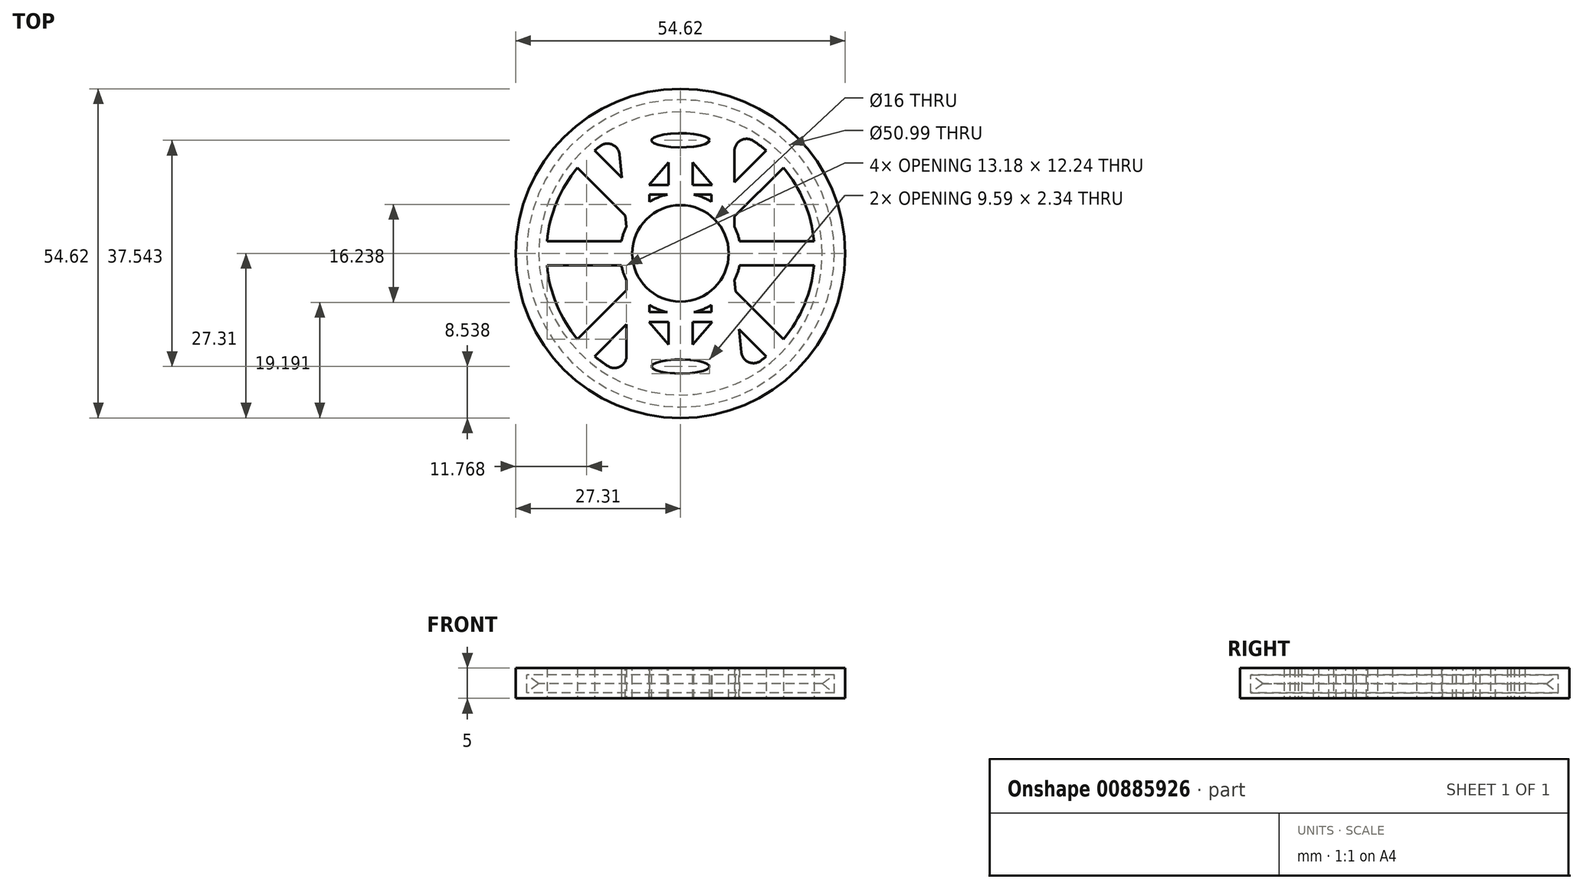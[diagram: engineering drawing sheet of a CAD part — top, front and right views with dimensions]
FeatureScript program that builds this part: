
annotation { "Feature Type Name" : "Feature", "Feature Type Description" : "" }
export const myFeature = defineFeature(function(context is Context, id is Id, definition is map)
    precondition{}
    {
        {
            var Q0;
            Q0=qCreatedBy(makeId("Top.planeOp"),FACE);
            var sketch = newSketch(context, id + "F0", { "sketchPlane" : qUnion([Q0])});
            skCircle(sketch, "E0", {"center": v(0, 0) * mm, "radius": 27.3 * mm});
            skCircle(sketch, "E1", {"center": v(0, 0) * mm, "radius": 3.12 * mm});
            skArc(sketch, "E2", {"start": v(-8.95, 4.46) * mm, "mid": v(-10, 0) * mm, "end": v(-8.95, -4.46) * mm});
            skArc(sketch, "E3.0", {"start": v(-13.28, 17.82) * mm, "mid": v(-22.21, -0.76) * mm, "end": v(-12.03, -18.69) * mm});
            skLineSegment(sketch, "E4.0", {"start": v(-10.1, 16.4) * mm, "end": v(-8.95, 4.46) * mm});
            skLineSegment(sketch, "E5.0", {"start": v(8.95, 17) * mm, "end": v(8.95, 4.46) * mm});
            skPoint(sketch, "E6.orphan", {"position": v(0, 22.46) * mm});
            skPoint(sketch, "E7.visualSharp", {"position": v(-10.4, 19.64) * mm});
            skArc(sketch, "E7.filletArc", {"start": v(-10.1, 16.4) * mm, "mid": v(-11.28, 18.04) * mm, "end": v(-13.28, 17.82) * mm});
            skPoint(sketch, "E8.visualSharp", {"position": v(8.95, 20.34) * mm});
            skArc(sketch, "E8.filletArc", {"start": v(12.03, 18.69) * mm, "mid": v(10, 18.76) * mm, "end": v(8.95, 17) * mm});
            skArc(sketch, "E9.1.0", {"start": v(-12.03, -18.69) * mm, "mid": v(-10, -18.76) * mm, "end": v(-8.95, -17) * mm});
            skArc(sketch, "E9.1.1", {"start": v(10.1, -16.4) * mm, "mid": v(11.28, -18.04) * mm, "end": v(13.28, -17.82) * mm});
            skLineSegment(sketch, "E9.1.2", {"start": v(10.1, -16.4) * mm, "end": v(8.95, -4.46) * mm});
            skLineSegment(sketch, "E9.1.3", {"start": v(-8.95, -17) * mm, "end": v(-8.95, -4.46) * mm});
            skArc(sketch, "E10.trimOffspring", {"start": v(13.28, -17.82) * mm, "mid": v(22.21, 0.76) * mm, "end": v(12.03, 18.69) * mm});
            skArc(sketch, "E11.trimOffspring", {"start": v(8.95, -4.46) * mm, "mid": v(10, 0) * mm, "end": v(8.95, 4.46) * mm});
            skSolve(sketch);
        }
        {
            var Q0;
            Q0=makeQuery(id+"F0.imprint","IMPRINT",FACE,{"disambiguationData":[TD([[makeQuery(id+"F0.imprint","IMPRINT",EDGE,{"derivedFrom":sQuery(id+"F0.wireOp",EDGE,"E0")}),1.0]])]});
            extrude(context, id + "F1", {"entities" : qUnion([Q0]), "depth" : 5 * mm, "offsetDistance" : 25.4 * mm});
        }
        {
            var Q0;
            Q0=makeQuery(id+"F1.opExtrude","CAP_FACE",FACE,{"disambiguationData":[OSD([sQuery(id+"F0.wireOp",EDGE,"E0"),sQuery(id+"F0.wireOp",EDGE,"E1"),sQuery(id+"F0.wireOp",EDGE,"E2"),sQuery(id+"F0.wireOp",EDGE,"E3.0"),sQuery(id+"F0.wireOp",EDGE,"E4.0"),sQuery(id+"F0.wireOp",EDGE,"E5.0"),sQuery(id+"F0.wireOp",EDGE,"E7.filletArc"),sQuery(id+"F0.wireOp",EDGE,"E8.filletArc"),sQuery(id+"F0.wireOp",EDGE,"E9.1.0"),sQuery(id+"F0.wireOp",EDGE,"E9.1.1"),sQuery(id+"F0.wireOp",EDGE,"E9.1.2"),sQuery(id+"F0.wireOp",EDGE,"E9.1.3"),sQuery(id+"F0.wireOp",EDGE,"E10.trimOffspring"),sQuery(id+"F0.wireOp",EDGE,"E11.trimOffspring")])],"isStart":false});
            var sketch = newSketch(context, id + "F2", { "sketchPlane" : qUnion([Q0])});
            skCircle(sketch, "E12", {"center": v(0, 0) * mm, "radius": 7.5 * mm});
            skSolve(sketch);
        }
        {
            var Q0;
            Q0=makeQuery(id+"F2.imprint","IMPRINT",FACE,{"disambiguationData":[TD([[makeQuery(id+"F2.imprint","IMPRINT",EDGE,{"derivedFrom":sQuery(id+"F2.wireOp",EDGE,"E12")}),1.0]])]});
            extrude(context, id + "F3", {"entities" : qUnion([Q0]), "operationType" : NewBodyOperationType.ADD, "depth" : 4 * mm, "offsetDistance" : 25.4 * mm});
        }
        {
            var Q0;
            Q0=qCreatedBy(makeId("Front.planeOp"),FACE);
            var sketch = newSketch(context, id + "F4", { "sketchPlane" : qUnion([Q0])});
            skCircle(sketch, "E13", {"center": v(-9.47, 12.31) * mm, "radius": 6.1 * mm});
            skLineSegment(sketch, "E14", {"start": v(0, 13.25) * mm, "end": v(0, -3.15) * mm, "construction": true});
            skSolve(sketch);
        }
        {
            var Q0;
            Q0=makeQuery(id+"F4.imprint","IMPRINT",FACE,{"disambiguationData":[TD([[makeQuery(id+"F4.imprint","IMPRINT",EDGE,{"derivedFrom":sQuery(id+"F4.wireOp",EDGE,"E13")}),1.0]])]});
            var Q1;
            Q1=sQuery(id+"F4.wireOp",EDGE,"E14");
            revolve(context, id + "F5", {"operationType" : NewBodyOperationType.REMOVE, "surfaceOperationType" : NewSurfaceOperationType.NEW, "entities" : qUnion([Q0]), "axis" : qUnion([Q1]), "revolveType" : RevolveType.FULL, "oppositeDirection" : true});
        }
        {
            var Q0;
            Q0=makeQuery(id+"F1.opExtrude","CAP_FACE",FACE,{"disambiguationData":[OSD([sQuery(id+"F0.wireOp",EDGE,"E0"),sQuery(id+"F0.wireOp",EDGE,"E1"),sQuery(id+"F0.wireOp",EDGE,"E2"),sQuery(id+"F0.wireOp",EDGE,"E3.0"),sQuery(id+"F0.wireOp",EDGE,"E4.0"),sQuery(id+"F0.wireOp",EDGE,"E5.0"),sQuery(id+"F0.wireOp",EDGE,"E7.filletArc"),sQuery(id+"F0.wireOp",EDGE,"E8.filletArc"),sQuery(id+"F0.wireOp",EDGE,"E9.1.0"),sQuery(id+"F0.wireOp",EDGE,"E9.1.1"),sQuery(id+"F0.wireOp",EDGE,"E9.1.2"),sQuery(id+"F0.wireOp",EDGE,"E9.1.3"),sQuery(id+"F0.wireOp",EDGE,"E10.trimOffspring"),sQuery(id+"F0.wireOp",EDGE,"E11.trimOffspring")])],"isStart":false});
            var sketch = newSketch(context, id + "F6", { "sketchPlane" : qUnion([Q0])});
            skLineSegment(sketch, "E15", {"start": v(0, 11.36) * mm, "end": v(-5.23, 11.36) * mm});
            skLineSegment(sketch, "E16", {"start": v(-5.23, 11.36) * mm, "end": v(0, 17.41) * mm});
            skLineSegment(sketch, "E17", {"start": v(0, 17.41) * mm, "end": v(0, 11.36) * mm});
            skLineSegment(sketch, "E18.MirrorCS", {"start": v(0, 11.36) * mm, "end": v(5.23, 11.36) * mm});
            skLineSegment(sketch, "E19.MirrorCS", {"start": v(5.23, 11.36) * mm, "end": v(0, 17.41) * mm});
            skLineSegment(sketch, "E20.1.0", {"start": v(-5.23, -11.36) * mm, "end": v(0, -17.41) * mm});
            skLineSegment(sketch, "E20.1.1", {"start": v(5.23, -11.36) * mm, "end": v(0, -17.41) * mm});
            skLineSegment(sketch, "E20.1.2", {"start": v(0, -11.36) * mm, "end": v(-5.23, -11.36) * mm});
            skLineSegment(sketch, "E20.1.3", {"start": v(0, -11.36) * mm, "end": v(5.23, -11.36) * mm});
            skPoint(sketch, "E20.center", {"position": v(0, 0) * mm});
            skSolve(sketch);
        }
        {
            var Q0;
            Q0=makeQuery(id+"F6.imprint","IMPRINT",FACE,{"disambiguationData":[TD([[makeQuery(id+"F6.imprint","IMPRINT",EDGE,{"derivedFrom":sQuery(id+"F6.wireOp",EDGE,"E17")}),1.0]])]});
            var Q1;
            Q1=makeQuery(id+"F6.imprint","IMPRINT",FACE,{"disambiguationData":[TD([[makeQuery(id+"F6.imprint","IMPRINT",EDGE,{"derivedFrom":sQuery(id+"F6.wireOp",EDGE,"E15")}),-1.0]])]});
            var Q2;
            Q2=makeQuery(id+"F6.imprint","IMPRINT",FACE,{"disambiguationData":[TD([[makeQuery(id+"F6.imprint","IMPRINT",EDGE,{"derivedFrom":sQuery(id+"F6.wireOp",EDGE,"E20.1.0")}),1.0]])]});
            extrude(context, id + "F7", {"entities" : qUnion([Q0, Q1, Q2]), "operationType" : NewBodyOperationType.REMOVE, "endBound" : BoundingType.THROUGH_ALL, "oppositeDirection" : true, "depth" : 25.4 * mm, "offsetDistance" : 25.4 * mm});
        }
        {
            var Q0;
            Q0=qCreatedBy(makeId("Front.planeOp"),FACE);
            var sketch = newSketch(context, id + "F8", { "sketchPlane" : qUnion([Q0])});
            skLineSegment(sketch, "E21", {"start": v(-25.5, 2.4) * mm, "end": v(-23.5, 2.4) * mm});
            skLineSegment(sketch, "E22", {"start": v(-23.5, 2.4) * mm, "end": v(-25.5, 0.9) * mm});
            skLineSegment(sketch, "E23", {"start": v(-25.5, 0.9) * mm, "end": v(-25.5, 2.4) * mm});
            skLineSegment(sketch, "E24.MirrorCS", {"start": v(-23.5, 2.4) * mm, "end": v(-25.5, 3.9) * mm});
            skLineSegment(sketch, "E25.MirrorCS", {"start": v(-25.5, 3.9) * mm, "end": v(-25.5, 2.4) * mm});
            skLineSegment(sketch, "E26", {"start": v(0, 41.08) * mm, "end": v(0, 0) * mm, "construction": true});
            skSolve(sketch);
        }
        {
            var Q0;
            Q0=qSketchRegion(id+"F8",true);
            var Q1;
            Q1=sQuery(id+"F8.wireOp",EDGE,"E26");
            revolve(context, id + "F9", {"operationType" : NewBodyOperationType.REMOVE, "surfaceOperationType" : NewSurfaceOperationType.NEW, "entities" : qUnion([Q0]), "axis" : qUnion([Q1]), "revolveType" : RevolveType.FULL});
        }
        {
            var Q0;
            Q0=makeQuery(id+"F0.imprint","IMPRINT",FACE,{"disambiguationData":[TD([[makeQuery(id+"F0.imprint","IMPRINT",EDGE,{"derivedFrom":sQuery(id+"F0.wireOp",EDGE,"E5.0")}),1.0]])]});
            var sketch = newSketch(context, id + "F10", { "sketchPlane" : qUnion([Q0])});
            skCircle(sketch, "E27", {"center": v(0, 5.74) * mm, "radius": 0.66 * mm});
            skCircle(sketch, "E28.1.0", {"center": v(-4.06, 4.06) * mm, "radius": 0.66 * mm});
            skCircle(sketch, "E28.2.0", {"center": v(-5.74, 0) * mm, "radius": 0.66 * mm});
            skPoint(sketch, "E28.center", {"position": v(0, 0) * mm});
            skCircle(sketch, "E29.1.3.0", {"center": v(-4.06, -4.06) * mm, "radius": 0.66 * mm});
            skCircle(sketch, "E29.1.4.0", {"center": v(0, -5.74) * mm, "radius": 0.66 * mm});
            skCircle(sketch, "E29.1.5.0", {"center": v(4.06, -4.06) * mm, "radius": 0.66 * mm});
            skCircle(sketch, "E29.1.6.0", {"center": v(5.74, 0) * mm, "radius": 0.66 * mm});
            skCircle(sketch, "E30.1.7.0", {"center": v(4.06, 4.06) * mm, "radius": 0.66 * mm});
            skSolve(sketch);
        }
        {
            var Q0;
            Q0=qSketchRegion(id+"F10",true);
            extrude(context, id + "F11", {"entities" : qUnion([Q0]), "operationType" : NewBodyOperationType.REMOVE, "endBound" : BoundingType.THROUGH_ALL, "depth" : 25.4 * mm, "offsetDistance" : 25.4 * mm});
        }
        {
            var Q0;
            Q0=qCreatedBy(makeId("Top.planeOp"),FACE);
            var sketch = newSketch(context, id + "F12", { "sketchPlane" : qUnion([Q0])});
            skLineSegment(sketch, "E31.0", {"start": v(-22.45, -2) * mm, "end": v(-8.8, -2) * mm});
            skLineSegment(sketch, "E32.0", {"start": v(-22.45, 2) * mm, "end": v(-8.8, 2) * mm});
            skPoint(sketch, "E33.start.orphan", {"position": v(-22.45, 0) * mm});
            skLineSegment(sketch, "E34", {"start": v(-8.8, -2) * mm, "end": v(-8.8, 2) * mm});
            skLineSegment(sketch, "E35", {"start": v(-22.45, -2) * mm, "end": v(-22.45, 2) * mm});
            skLineSegment(sketch, "E36.1.0", {"start": v(-4.8, -7.64) * mm, "end": v(-7.64, -4.8) * mm});
            skLineSegment(sketch, "E36.1.1", {"start": v(-14.46, -17.29) * mm, "end": v(-4.8, -7.64) * mm});
            skLineSegment(sketch, "E36.1.2", {"start": v(-17.29, -14.46) * mm, "end": v(-7.64, -4.8) * mm});
            skLineSegment(sketch, "E36.1.3", {"start": v(-14.46, -17.29) * mm, "end": v(-17.29, -14.46) * mm});
            skLineSegment(sketch, "E36.2.0", {"start": v(2, -8.8) * mm, "end": v(-2, -8.8) * mm});
            skLineSegment(sketch, "E36.2.1", {"start": v(2, -22.45) * mm, "end": v(2, -8.8) * mm});
            skLineSegment(sketch, "E36.2.2", {"start": v(-2, -22.45) * mm, "end": v(-2, -8.8) * mm});
            skLineSegment(sketch, "E36.2.3", {"start": v(2, -22.45) * mm, "end": v(-2, -22.45) * mm});
            skPoint(sketch, "E36.center", {"position": v(0, 0) * mm});
            skLineSegment(sketch, "E37.1.3.0", {"start": v(7.64, -4.8) * mm, "end": v(4.8, -7.64) * mm});
            skLineSegment(sketch, "E37.3.3.0", {"start": v(17.29, -14.46) * mm, "end": v(7.64, -4.8) * mm});
            skLineSegment(sketch, "E37.6.3.0", {"start": v(14.46, -17.29) * mm, "end": v(4.8, -7.64) * mm});
            skLineSegment(sketch, "E37.9.3.0", {"start": v(17.29, -14.46) * mm, "end": v(14.46, -17.29) * mm});
            skLineSegment(sketch, "E38.1.4.0", {"start": v(8.8, 2) * mm, "end": v(8.8, -2) * mm});
            skLineSegment(sketch, "E38.3.4.0", {"start": v(22.45, 2) * mm, "end": v(8.8, 2) * mm});
            skLineSegment(sketch, "E38.6.4.0", {"start": v(22.45, -2) * mm, "end": v(8.8, -2) * mm});
            skLineSegment(sketch, "E38.9.4.0", {"start": v(22.45, 2) * mm, "end": v(22.45, -2) * mm});
            skLineSegment(sketch, "E38.1.5.0", {"start": v(4.8, 7.64) * mm, "end": v(7.64, 4.8) * mm});
            skLineSegment(sketch, "E38.3.5.0", {"start": v(14.46, 17.29) * mm, "end": v(4.8, 7.64) * mm});
            skLineSegment(sketch, "E38.6.5.0", {"start": v(17.29, 14.46) * mm, "end": v(7.64, 4.8) * mm});
            skLineSegment(sketch, "E38.9.5.0", {"start": v(14.46, 17.29) * mm, "end": v(17.29, 14.46) * mm});
            skLineSegment(sketch, "E39.1.6.0", {"start": v(-2, 8.8) * mm, "end": v(2, 8.8) * mm});
            skLineSegment(sketch, "E39.3.6.0", {"start": v(-2, 22.45) * mm, "end": v(-2, 8.8) * mm});
            skLineSegment(sketch, "E39.6.6.0", {"start": v(2, 22.45) * mm, "end": v(2, 8.8) * mm});
            skLineSegment(sketch, "E39.9.6.0", {"start": v(-2, 22.45) * mm, "end": v(2, 22.45) * mm});
            skLineSegment(sketch, "E39.1.7.0", {"start": v(-7.64, 4.8) * mm, "end": v(-4.8, 7.64) * mm});
            skLineSegment(sketch, "E39.3.7.0", {"start": v(-17.29, 14.46) * mm, "end": v(-7.64, 4.8) * mm});
            skLineSegment(sketch, "E39.6.7.0", {"start": v(-14.46, 17.29) * mm, "end": v(-4.8, 7.64) * mm});
            skLineSegment(sketch, "E39.9.7.0", {"start": v(-17.29, 14.46) * mm, "end": v(-14.46, 17.29) * mm});
            skSolve(sketch);
        }
        {
            var Q0;
            Q0=qSketchRegion(id+"F12",true);
            extrude(context, id + "F13", {"entities" : qUnion([Q0]), "operationType" : NewBodyOperationType.ADD, "depth" : 5 * mm, "offsetDistance" : 25.4 * mm});
        }
        {
            var Q0;
            Q0=qCreatedBy(makeId("Top.planeOp"),FACE);
            var sketch = newSketch(context, id + "F14", { "sketchPlane" : qUnion([Q0])});
            skEllipse(sketch, "E40", {"center": v(0, 18.77) * mm, "majorRadius": 4.8 * mm, "minorRadius": 1.17 * mm, "majorAxis": v(1, 0)});
            skEllipse(sketch, "E41.1.0", {"center": v(0, -18.77) * mm, "majorRadius": 4.8 * mm, "minorRadius": 1.17 * mm, "majorAxis": v(-1, 0)});
            skPoint(sketch, "E41.center", {"position": v(0, 0) * mm});
            skSolve(sketch);
        }
        {
            var Q0;
            Q0=qSketchRegion(id+"F14",true);
            extrude(context, id + "F15", {"entities" : qUnion([Q0]), "operationType" : NewBodyOperationType.REMOVE, "endBound" : BoundingType.SYMMETRIC, "oppositeDirection" : true, "depth" : 25.4 * mm, "offsetDistance" : 25.4 * mm});
        }
        {
            var Q0;
            Q0=qCreatedBy(makeId("Top.planeOp"),FACE);
            var sketch = newSketch(context, id + "F16", { "sketchPlane" : qUnion([Q0])});
            skLineSegment(sketch, "E42.bottom", {"start": v(5.15, 9.76) * mm, "end": v(-5.15, 9.76) * mm});
            skLineSegment(sketch, "E42.top", {"start": v(5.15, 8.51) * mm, "end": v(-5.15, 8.51) * mm});
            skLineSegment(sketch, "E42.left", {"start": v(5.15, 9.76) * mm, "end": v(5.15, 8.51) * mm});
            skLineSegment(sketch, "E42.right", {"start": v(-5.15, 9.76) * mm, "end": v(-5.15, 8.51) * mm});
            skPoint(sketch, "E42.middle", {"position": v(0, 9.13) * mm});
            skLineSegment(sketch, "E43.1.0", {"start": v(-5.15, -9.76) * mm, "end": v(-5.15, -8.51) * mm});
            skLineSegment(sketch, "E43.1.1", {"start": v(5.15, -9.76) * mm, "end": v(5.15, -8.51) * mm});
            skLineSegment(sketch, "E43.1.2", {"start": v(-5.15, -8.51) * mm, "end": v(5.15, -8.51) * mm});
            skLineSegment(sketch, "E43.1.3", {"start": v(-5.15, -9.76) * mm, "end": v(5.15, -9.76) * mm});
            skPoint(sketch, "E43.center", {"position": v(0, 0) * mm});
            skSolve(sketch);
        }
        {
            var Q0;
            Q0=qSketchRegion(id+"F16",true);
            extrude(context, id + "F17", {"entities" : qUnion([Q0]), "operationType" : NewBodyOperationType.REMOVE, "endBound" : BoundingType.SYMMETRIC, "oppositeDirection" : true, "depth" : 25.4 * mm, "offsetDistance" : 25.4 * mm});
        }
        {
            var Q0;
            Q0=makeQuery(id+"F13.boolean.opBoolean","MERGE",FACE,{"derivedFrom":[makeQuery(id+"F1.opExtrude","CAP_FACE",FACE,{"disambiguationData":[OSD([sQuery(id+"F0.wireOp",EDGE,"E0"),sQuery(id+"F0.wireOp",EDGE,"E1"),sQuery(id+"F0.wireOp",EDGE,"E2"),sQuery(id+"F0.wireOp",EDGE,"E3.0"),sQuery(id+"F0.wireOp",EDGE,"E4.0"),sQuery(id+"F0.wireOp",EDGE,"E5.0"),sQuery(id+"F0.wireOp",EDGE,"E7.filletArc"),sQuery(id+"F0.wireOp",EDGE,"E8.filletArc"),sQuery(id+"F0.wireOp",EDGE,"E9.1.0"),sQuery(id+"F0.wireOp",EDGE,"E9.1.1"),sQuery(id+"F0.wireOp",EDGE,"E9.1.2"),sQuery(id+"F0.wireOp",EDGE,"E9.1.3"),sQuery(id+"F0.wireOp",EDGE,"E10.trimOffspring"),sQuery(id+"F0.wireOp",EDGE,"E11.trimOffspring")])],"isStart":false}),makeQuery(id+"F13.opExtrude","CAP_FACE",FACE,{"disambiguationData":[OSD([sQuery(id+"F12.wireOp",EDGE,"E31.0"),sQuery(id+"F12.wireOp",EDGE,"E32.0"),sQuery(id+"F12.wireOp",EDGE,"E34"),sQuery(id+"F12.wireOp",EDGE,"E35")])],"isStart":false}),makeQuery(id+"F13.opExtrude","CAP_FACE",FACE,{"disambiguationData":[OSD([sQuery(id+"F12.wireOp",EDGE,"E36.1.0"),sQuery(id+"F12.wireOp",EDGE,"E36.1.1"),sQuery(id+"F12.wireOp",EDGE,"E36.1.2"),sQuery(id+"F12.wireOp",EDGE,"E36.1.3")])],"isStart":false}),makeQuery(id+"F13.opExtrude","CAP_FACE",FACE,{"disambiguationData":[OSD([sQuery(id+"F12.wireOp",EDGE,"E36.2.0"),sQuery(id+"F12.wireOp",EDGE,"E36.2.1"),sQuery(id+"F12.wireOp",EDGE,"E36.2.2"),sQuery(id+"F12.wireOp",EDGE,"E36.2.3")])],"isStart":false}),makeQuery(id+"F13.opExtrude","CAP_FACE",FACE,{"disambiguationData":[OSD([sQuery(id+"F12.wireOp",EDGE,"E37.1.3.0"),sQuery(id+"F12.wireOp",EDGE,"E37.3.3.0"),sQuery(id+"F12.wireOp",EDGE,"E37.6.3.0"),sQuery(id+"F12.wireOp",EDGE,"E37.9.3.0")])],"isStart":false}),makeQuery(id+"F13.opExtrude","CAP_FACE",FACE,{"disambiguationData":[OSD([sQuery(id+"F12.wireOp",EDGE,"E38.1.4.0"),sQuery(id+"F12.wireOp",EDGE,"E38.3.4.0"),sQuery(id+"F12.wireOp",EDGE,"E38.6.4.0"),sQuery(id+"F12.wireOp",EDGE,"E38.9.4.0")])],"isStart":false}),makeQuery(id+"F13.opExtrude","CAP_FACE",FACE,{"disambiguationData":[OSD([sQuery(id+"F12.wireOp",EDGE,"E38.1.5.0"),sQuery(id+"F12.wireOp",EDGE,"E38.3.5.0"),sQuery(id+"F12.wireOp",EDGE,"E38.6.5.0"),sQuery(id+"F12.wireOp",EDGE,"E38.9.5.0")])],"isStart":false}),makeQuery(id+"F13.opExtrude","CAP_FACE",FACE,{"disambiguationData":[OSD([sQuery(id+"F12.wireOp",EDGE,"E39.1.6.0"),sQuery(id+"F12.wireOp",EDGE,"E39.3.6.0"),sQuery(id+"F12.wireOp",EDGE,"E39.6.6.0"),sQuery(id+"F12.wireOp",EDGE,"E39.9.6.0")])],"isStart":false}),makeQuery(id+"F13.opExtrude","CAP_FACE",FACE,{"disambiguationData":[OSD([sQuery(id+"F12.wireOp",EDGE,"E39.1.7.0"),sQuery(id+"F12.wireOp",EDGE,"E39.3.7.0"),sQuery(id+"F12.wireOp",EDGE,"E39.6.7.0"),sQuery(id+"F12.wireOp",EDGE,"E39.9.7.0")])],"isStart":false})]});
            var sketch = newSketch(context, id + "F18", { "sketchPlane" : qUnion([Q0])});
            skCircle(sketch, "E44", {"center": v(0, 0) * mm, "radius": 8 * mm});
            skSolve(sketch);
        }
        {
            var Q0;
            Q0 = qSketchRegion(id + "F18", true);
            extrude(context, id + "F19", {"entities" : qUnion([Q0]), "operationType" : NewBodyOperationType.REMOVE, "endBound" : BoundingType.SYMMETRIC, "oppositeDirection" : true, "depth" : 25.4 * mm, "offsetDistance" : 25.4 * mm});
        }
        {
            var Q0;
            Q0=makeQuery(id+"F13.boolean.opBoolean","MERGE",FACE,{"derivedFrom":[makeQuery(id+"F1.opExtrude","CAP_FACE",FACE,{"disambiguationData":[OSD([sQuery(id+"F0.wireOp",EDGE,"E0"),sQuery(id+"F0.wireOp",EDGE,"E1"),sQuery(id+"F0.wireOp",EDGE,"E2"),sQuery(id+"F0.wireOp",EDGE,"E3.0"),sQuery(id+"F0.wireOp",EDGE,"E4.0"),sQuery(id+"F0.wireOp",EDGE,"E5.0"),sQuery(id+"F0.wireOp",EDGE,"E7.filletArc"),sQuery(id+"F0.wireOp",EDGE,"E8.filletArc"),sQuery(id+"F0.wireOp",EDGE,"E9.1.0"),sQuery(id+"F0.wireOp",EDGE,"E9.1.1"),sQuery(id+"F0.wireOp",EDGE,"E9.1.2"),sQuery(id+"F0.wireOp",EDGE,"E9.1.3"),sQuery(id+"F0.wireOp",EDGE,"E10.trimOffspring"),sQuery(id+"F0.wireOp",EDGE,"E11.trimOffspring")])],"isStart":false}),makeQuery(id+"F13.opExtrude","CAP_FACE",FACE,{"disambiguationData":[OSD([sQuery(id+"F12.wireOp",EDGE,"E31.0"),sQuery(id+"F12.wireOp",EDGE,"E32.0"),sQuery(id+"F12.wireOp",EDGE,"E34"),sQuery(id+"F12.wireOp",EDGE,"E35")])],"isStart":false}),makeQuery(id+"F13.opExtrude","CAP_FACE",FACE,{"disambiguationData":[OSD([sQuery(id+"F12.wireOp",EDGE,"E36.1.0"),sQuery(id+"F12.wireOp",EDGE,"E36.1.1"),sQuery(id+"F12.wireOp",EDGE,"E36.1.2"),sQuery(id+"F12.wireOp",EDGE,"E36.1.3")])],"isStart":false}),makeQuery(id+"F13.opExtrude","CAP_FACE",FACE,{"disambiguationData":[OSD([sQuery(id+"F12.wireOp",EDGE,"E36.2.0"),sQuery(id+"F12.wireOp",EDGE,"E36.2.1"),sQuery(id+"F12.wireOp",EDGE,"E36.2.2"),sQuery(id+"F12.wireOp",EDGE,"E36.2.3")])],"isStart":false}),makeQuery(id+"F13.opExtrude","CAP_FACE",FACE,{"disambiguationData":[OSD([sQuery(id+"F12.wireOp",EDGE,"E37.1.3.0"),sQuery(id+"F12.wireOp",EDGE,"E37.3.3.0"),sQuery(id+"F12.wireOp",EDGE,"E37.6.3.0"),sQuery(id+"F12.wireOp",EDGE,"E37.9.3.0")])],"isStart":false}),makeQuery(id+"F13.opExtrude","CAP_FACE",FACE,{"disambiguationData":[OSD([sQuery(id+"F12.wireOp",EDGE,"E38.1.4.0"),sQuery(id+"F12.wireOp",EDGE,"E38.3.4.0"),sQuery(id+"F12.wireOp",EDGE,"E38.6.4.0"),sQuery(id+"F12.wireOp",EDGE,"E38.9.4.0")])],"isStart":false}),makeQuery(id+"F13.opExtrude","CAP_FACE",FACE,{"disambiguationData":[OSD([sQuery(id+"F12.wireOp",EDGE,"E38.1.5.0"),sQuery(id+"F12.wireOp",EDGE,"E38.3.5.0"),sQuery(id+"F12.wireOp",EDGE,"E38.6.5.0"),sQuery(id+"F12.wireOp",EDGE,"E38.9.5.0")])],"isStart":false}),makeQuery(id+"F13.opExtrude","CAP_FACE",FACE,{"disambiguationData":[OSD([sQuery(id+"F12.wireOp",EDGE,"E39.1.6.0"),sQuery(id+"F12.wireOp",EDGE,"E39.3.6.0"),sQuery(id+"F12.wireOp",EDGE,"E39.6.6.0"),sQuery(id+"F12.wireOp",EDGE,"E39.9.6.0")])],"isStart":false}),makeQuery(id+"F13.opExtrude","CAP_FACE",FACE,{"disambiguationData":[OSD([sQuery(id+"F12.wireOp",EDGE,"E39.1.7.0"),sQuery(id+"F12.wireOp",EDGE,"E39.3.7.0"),sQuery(id+"F12.wireOp",EDGE,"E39.6.7.0"),sQuery(id+"F12.wireOp",EDGE,"E39.9.7.0")])],"isStart":false})]});
            var sketch = newSketch(context, id + "F20", { "sketchPlane" : qUnion([Q0])});
            skCircle(sketch, "E45", {"center": v(0, 0) * mm, "radius": 10 * mm});
            skSolve(sketch);
        }
        {
            var Q0;
            {var subQ0=sQuery(id+"F20.wireOp",EDGE,"E45");var subQ1=makeQuery(id+"F17.boolean.opBoolean","INTERSECT",EDGE,{"derivedFrom":[makeQuery(id+"F13.boolean.opBoolean","MERGE",FACE,{"derivedFrom":[makeQuery(id+"F1.opExtrude","CAP_FACE",FACE,{"disambiguationData":[OSD([sQuery(id+"F0.wireOp",EDGE,"E0"),sQuery(id+"F0.wireOp",EDGE,"E1"),sQuery(id+"F0.wireOp",EDGE,"E2"),sQuery(id+"F0.wireOp",EDGE,"E3.0"),sQuery(id+"F0.wireOp",EDGE,"E4.0"),sQuery(id+"F0.wireOp",EDGE,"E5.0"),sQuery(id+"F0.wireOp",EDGE,"E7.filletArc"),sQuery(id+"F0.wireOp",EDGE,"E8.filletArc"),sQuery(id+"F0.wireOp",EDGE,"E9.1.0"),sQuery(id+"F0.wireOp",EDGE,"E9.1.1"),sQuery(id+"F0.wireOp",EDGE,"E9.1.2"),sQuery(id+"F0.wireOp",EDGE,"E9.1.3"),sQuery(id+"F0.wireOp",EDGE,"E10.trimOffspring"),sQuery(id+"F0.wireOp",EDGE,"E11.trimOffspring")])],"isStart":false}),makeQuery(id+"F13.opExtrude","CAP_FACE",FACE,{"disambiguationData":[OSD([sQuery(id+"F12.wireOp",EDGE,"E31.0"),sQuery(id+"F12.wireOp",EDGE,"E32.0"),sQuery(id+"F12.wireOp",EDGE,"E34"),sQuery(id+"F12.wireOp",EDGE,"E35")])],"isStart":false}),makeQuery(id+"F13.opExtrude","CAP_FACE",FACE,{"disambiguationData":[OSD([sQuery(id+"F12.wireOp",EDGE,"E36.1.0"),sQuery(id+"F12.wireOp",EDGE,"E36.1.1"),sQuery(id+"F12.wireOp",EDGE,"E36.1.2"),sQuery(id+"F12.wireOp",EDGE,"E36.1.3")])],"isStart":false}),makeQuery(id+"F13.opExtrude","CAP_FACE",FACE,{"disambiguationData":[OSD([sQuery(id+"F12.wireOp",EDGE,"E36.2.0"),sQuery(id+"F12.wireOp",EDGE,"E36.2.1"),sQuery(id+"F12.wireOp",EDGE,"E36.2.2"),sQuery(id+"F12.wireOp",EDGE,"E36.2.3")])],"isStart":false}),makeQuery(id+"F13.opExtrude","CAP_FACE",FACE,{"disambiguationData":[OSD([sQuery(id+"F12.wireOp",EDGE,"E37.1.3.0"),sQuery(id+"F12.wireOp",EDGE,"E37.3.3.0"),sQuery(id+"F12.wireOp",EDGE,"E37.6.3.0"),sQuery(id+"F12.wireOp",EDGE,"E37.9.3.0")])],"isStart":false}),makeQuery(id+"F13.opExtrude","CAP_FACE",FACE,{"disambiguationData":[OSD([sQuery(id+"F12.wireOp",EDGE,"E38.1.4.0"),sQuery(id+"F12.wireOp",EDGE,"E38.3.4.0"),sQuery(id+"F12.wireOp",EDGE,"E38.6.4.0"),sQuery(id+"F12.wireOp",EDGE,"E38.9.4.0")])],"isStart":false}),makeQuery(id+"F13.opExtrude","CAP_FACE",FACE,{"disambiguationData":[OSD([sQuery(id+"F12.wireOp",EDGE,"E38.1.5.0"),sQuery(id+"F12.wireOp",EDGE,"E38.3.5.0"),sQuery(id+"F12.wireOp",EDGE,"E38.6.5.0"),sQuery(id+"F12.wireOp",EDGE,"E38.9.5.0")])],"isStart":false}),makeQuery(id+"F13.opExtrude","CAP_FACE",FACE,{"disambiguationData":[OSD([sQuery(id+"F12.wireOp",EDGE,"E39.1.6.0"),sQuery(id+"F12.wireOp",EDGE,"E39.3.6.0"),sQuery(id+"F12.wireOp",EDGE,"E39.6.6.0"),sQuery(id+"F12.wireOp",EDGE,"E39.9.6.0")])],"isStart":false}),makeQuery(id+"F13.opExtrude","CAP_FACE",FACE,{"disambiguationData":[OSD([sQuery(id+"F12.wireOp",EDGE,"E39.1.7.0"),sQuery(id+"F12.wireOp",EDGE,"E39.3.7.0"),sQuery(id+"F12.wireOp",EDGE,"E39.6.7.0"),sQuery(id+"F12.wireOp",EDGE,"E39.9.7.0")])],"isStart":false})]}),makeQuery(id+"F17.opExtrude","SWEPT_FACE",FACE,{"disambiguationData":[OSD([sQuery(id+"F16.wireOp",EDGE,"E43.1.3")])]})]});var subQ2=makeQuery(id+"F20.imprint","INTERSECT",VERTEX,{"disambiguationData":[OD(0.0)],"derivedFrom":[subQ1,subQ0]});Q0=makeQuery(id+"F20.imprint","IMPRINT",FACE,{"disambiguationData":[TD([[makeQuery(id+"F20.imprint","IMPRINT",EDGE,{"disambiguationData":[TD([[subQ2,-1.0]])],"derivedFrom":subQ0}),1.0]])]});}
            var Q1;
            {var subQ1=makeQuery(id+"F13.boolean.opBoolean","MERGE",FACE,{"derivedFrom":[makeQuery(id+"F1.opExtrude","CAP_FACE",FACE,{"disambiguationData":[OSD([sQuery(id+"F0.wireOp",EDGE,"E0"),sQuery(id+"F0.wireOp",EDGE,"E1"),sQuery(id+"F0.wireOp",EDGE,"E2"),sQuery(id+"F0.wireOp",EDGE,"E3.0"),sQuery(id+"F0.wireOp",EDGE,"E4.0"),sQuery(id+"F0.wireOp",EDGE,"E5.0"),sQuery(id+"F0.wireOp",EDGE,"E7.filletArc"),sQuery(id+"F0.wireOp",EDGE,"E8.filletArc"),sQuery(id+"F0.wireOp",EDGE,"E9.1.0"),sQuery(id+"F0.wireOp",EDGE,"E9.1.1"),sQuery(id+"F0.wireOp",EDGE,"E9.1.2"),sQuery(id+"F0.wireOp",EDGE,"E9.1.3"),sQuery(id+"F0.wireOp",EDGE,"E10.trimOffspring"),sQuery(id+"F0.wireOp",EDGE,"E11.trimOffspring")])],"isStart":false}),makeQuery(id+"F13.opExtrude","CAP_FACE",FACE,{"disambiguationData":[OSD([sQuery(id+"F12.wireOp",EDGE,"E31.0"),sQuery(id+"F12.wireOp",EDGE,"E32.0"),sQuery(id+"F12.wireOp",EDGE,"E34"),sQuery(id+"F12.wireOp",EDGE,"E35")])],"isStart":false}),makeQuery(id+"F13.opExtrude","CAP_FACE",FACE,{"disambiguationData":[OSD([sQuery(id+"F12.wireOp",EDGE,"E36.1.0"),sQuery(id+"F12.wireOp",EDGE,"E36.1.1"),sQuery(id+"F12.wireOp",EDGE,"E36.1.2"),sQuery(id+"F12.wireOp",EDGE,"E36.1.3")])],"isStart":false}),makeQuery(id+"F13.opExtrude","CAP_FACE",FACE,{"disambiguationData":[OSD([sQuery(id+"F12.wireOp",EDGE,"E36.2.0"),sQuery(id+"F12.wireOp",EDGE,"E36.2.1"),sQuery(id+"F12.wireOp",EDGE,"E36.2.2"),sQuery(id+"F12.wireOp",EDGE,"E36.2.3")])],"isStart":false}),makeQuery(id+"F13.opExtrude","CAP_FACE",FACE,{"disambiguationData":[OSD([sQuery(id+"F12.wireOp",EDGE,"E37.1.3.0"),sQuery(id+"F12.wireOp",EDGE,"E37.3.3.0"),sQuery(id+"F12.wireOp",EDGE,"E37.6.3.0"),sQuery(id+"F12.wireOp",EDGE,"E37.9.3.0")])],"isStart":false}),makeQuery(id+"F13.opExtrude","CAP_FACE",FACE,{"disambiguationData":[OSD([sQuery(id+"F12.wireOp",EDGE,"E38.1.4.0"),sQuery(id+"F12.wireOp",EDGE,"E38.3.4.0"),sQuery(id+"F12.wireOp",EDGE,"E38.6.4.0"),sQuery(id+"F12.wireOp",EDGE,"E38.9.4.0")])],"isStart":false}),makeQuery(id+"F13.opExtrude","CAP_FACE",FACE,{"disambiguationData":[OSD([sQuery(id+"F12.wireOp",EDGE,"E38.1.5.0"),sQuery(id+"F12.wireOp",EDGE,"E38.3.5.0"),sQuery(id+"F12.wireOp",EDGE,"E38.6.5.0"),sQuery(id+"F12.wireOp",EDGE,"E38.9.5.0")])],"isStart":false}),makeQuery(id+"F13.opExtrude","CAP_FACE",FACE,{"disambiguationData":[OSD([sQuery(id+"F12.wireOp",EDGE,"E39.1.6.0"),sQuery(id+"F12.wireOp",EDGE,"E39.3.6.0"),sQuery(id+"F12.wireOp",EDGE,"E39.6.6.0"),sQuery(id+"F12.wireOp",EDGE,"E39.9.6.0")])],"isStart":false}),makeQuery(id+"F13.opExtrude","CAP_FACE",FACE,{"disambiguationData":[OSD([sQuery(id+"F12.wireOp",EDGE,"E39.1.7.0"),sQuery(id+"F12.wireOp",EDGE,"E39.3.7.0"),sQuery(id+"F12.wireOp",EDGE,"E39.6.7.0"),sQuery(id+"F12.wireOp",EDGE,"E39.9.7.0")])],"isStart":false})]});var subQ5=makeQuery(id+"F17.boolean.opBoolean","INTERSECT",EDGE,{"derivedFrom":[subQ1,makeQuery(id+"F17.opExtrude","SWEPT_FACE",FACE,{"disambiguationData":[OSD([sQuery(id+"F16.wireOp",EDGE,"E42.top")])]})]});Q1=makeQuery(id+"F20.imprint","IMPRINT",FACE,{"disambiguationData":[TD([[makeQuery(id+"F20.imprint","IMPRINT",EDGE,{"derivedFrom":subQ5}),-1.0]])]});}
            var Q2;
            {var subQ0=sQuery(id+"F20.wireOp",EDGE,"E45");var subQ20=sQuery(id+"F12.wireOp",EDGE,"E31.0");var subQ29=makeQuery(id+"F20.imprint","INTERSECT",VERTEX,{"derivedFrom":[makeQuery(id+"F13.opExtrude","CAP_EDGE",EDGE,{"disambiguationData":[OSD([subQ20])],"isStart":false}),subQ0]});Q2=makeQuery(id+"F20.imprint","IMPRINT",FACE,{"disambiguationData":[TD([[makeQuery(id+"F20.imprint","IMPRINT",EDGE,{"disambiguationData":[TD([[subQ29,1.0]])],"derivedFrom":subQ0}),1.0]])]});}
            var Q3;
            {var subQ0=makeQuery(id+"F13.boolean.opBoolean","MERGE",FACE,{"derivedFrom":[makeQuery(id+"F1.opExtrude","CAP_FACE",FACE,{"disambiguationData":[OSD([sQuery(id+"F0.wireOp",EDGE,"E0"),sQuery(id+"F0.wireOp",EDGE,"E1"),sQuery(id+"F0.wireOp",EDGE,"E2"),sQuery(id+"F0.wireOp",EDGE,"E3.0"),sQuery(id+"F0.wireOp",EDGE,"E4.0"),sQuery(id+"F0.wireOp",EDGE,"E5.0"),sQuery(id+"F0.wireOp",EDGE,"E7.filletArc"),sQuery(id+"F0.wireOp",EDGE,"E8.filletArc"),sQuery(id+"F0.wireOp",EDGE,"E9.1.0"),sQuery(id+"F0.wireOp",EDGE,"E9.1.1"),sQuery(id+"F0.wireOp",EDGE,"E9.1.2"),sQuery(id+"F0.wireOp",EDGE,"E9.1.3"),sQuery(id+"F0.wireOp",EDGE,"E10.trimOffspring"),sQuery(id+"F0.wireOp",EDGE,"E11.trimOffspring")])],"isStart":false}),makeQuery(id+"F13.opExtrude","CAP_FACE",FACE,{"disambiguationData":[OSD([sQuery(id+"F12.wireOp",EDGE,"E31.0"),sQuery(id+"F12.wireOp",EDGE,"E32.0"),sQuery(id+"F12.wireOp",EDGE,"E34"),sQuery(id+"F12.wireOp",EDGE,"E35")])],"isStart":false}),makeQuery(id+"F13.opExtrude","CAP_FACE",FACE,{"disambiguationData":[OSD([sQuery(id+"F12.wireOp",EDGE,"E36.1.0"),sQuery(id+"F12.wireOp",EDGE,"E36.1.1"),sQuery(id+"F12.wireOp",EDGE,"E36.1.2"),sQuery(id+"F12.wireOp",EDGE,"E36.1.3")])],"isStart":false}),makeQuery(id+"F13.opExtrude","CAP_FACE",FACE,{"disambiguationData":[OSD([sQuery(id+"F12.wireOp",EDGE,"E36.2.0"),sQuery(id+"F12.wireOp",EDGE,"E36.2.1"),sQuery(id+"F12.wireOp",EDGE,"E36.2.2"),sQuery(id+"F12.wireOp",EDGE,"E36.2.3")])],"isStart":false}),makeQuery(id+"F13.opExtrude","CAP_FACE",FACE,{"disambiguationData":[OSD([sQuery(id+"F12.wireOp",EDGE,"E37.1.3.0"),sQuery(id+"F12.wireOp",EDGE,"E37.3.3.0"),sQuery(id+"F12.wireOp",EDGE,"E37.6.3.0"),sQuery(id+"F12.wireOp",EDGE,"E37.9.3.0")])],"isStart":false}),makeQuery(id+"F13.opExtrude","CAP_FACE",FACE,{"disambiguationData":[OSD([sQuery(id+"F12.wireOp",EDGE,"E38.1.4.0"),sQuery(id+"F12.wireOp",EDGE,"E38.3.4.0"),sQuery(id+"F12.wireOp",EDGE,"E38.6.4.0"),sQuery(id+"F12.wireOp",EDGE,"E38.9.4.0")])],"isStart":false}),makeQuery(id+"F13.opExtrude","CAP_FACE",FACE,{"disambiguationData":[OSD([sQuery(id+"F12.wireOp",EDGE,"E38.1.5.0"),sQuery(id+"F12.wireOp",EDGE,"E38.3.5.0"),sQuery(id+"F12.wireOp",EDGE,"E38.6.5.0"),sQuery(id+"F12.wireOp",EDGE,"E38.9.5.0")])],"isStart":false}),makeQuery(id+"F13.opExtrude","CAP_FACE",FACE,{"disambiguationData":[OSD([sQuery(id+"F12.wireOp",EDGE,"E39.1.6.0"),sQuery(id+"F12.wireOp",EDGE,"E39.3.6.0"),sQuery(id+"F12.wireOp",EDGE,"E39.6.6.0"),sQuery(id+"F12.wireOp",EDGE,"E39.9.6.0")])],"isStart":false}),makeQuery(id+"F13.opExtrude","CAP_FACE",FACE,{"disambiguationData":[OSD([sQuery(id+"F12.wireOp",EDGE,"E39.1.7.0"),sQuery(id+"F12.wireOp",EDGE,"E39.3.7.0"),sQuery(id+"F12.wireOp",EDGE,"E39.6.7.0"),sQuery(id+"F12.wireOp",EDGE,"E39.9.7.0")])],"isStart":false})]});var subQ1=makeQuery(id+"F17.boolean.opBoolean","INTERSECT",EDGE,{"derivedFrom":[subQ0,makeQuery(id+"F17.opExtrude","SWEPT_FACE",FACE,{"disambiguationData":[OSD([sQuery(id+"F16.wireOp",EDGE,"E43.1.2")])]})]});Q3=makeQuery(id+"F20.imprint","IMPRINT",FACE,{"disambiguationData":[TD([[makeQuery(id+"F20.imprint","IMPRINT",EDGE,{"derivedFrom":subQ1}),-1.0]])]});}
            var Q4;
            {var subQ0=sQuery(id+"F20.wireOp",EDGE,"E45");var subQ1=makeQuery(id+"F17.boolean.opBoolean","INTERSECT",EDGE,{"derivedFrom":[makeQuery(id+"F13.boolean.opBoolean","MERGE",FACE,{"derivedFrom":[makeQuery(id+"F1.opExtrude","CAP_FACE",FACE,{"disambiguationData":[OSD([sQuery(id+"F0.wireOp",EDGE,"E0"),sQuery(id+"F0.wireOp",EDGE,"E1"),sQuery(id+"F0.wireOp",EDGE,"E2"),sQuery(id+"F0.wireOp",EDGE,"E3.0"),sQuery(id+"F0.wireOp",EDGE,"E4.0"),sQuery(id+"F0.wireOp",EDGE,"E5.0"),sQuery(id+"F0.wireOp",EDGE,"E7.filletArc"),sQuery(id+"F0.wireOp",EDGE,"E8.filletArc"),sQuery(id+"F0.wireOp",EDGE,"E9.1.0"),sQuery(id+"F0.wireOp",EDGE,"E9.1.1"),sQuery(id+"F0.wireOp",EDGE,"E9.1.2"),sQuery(id+"F0.wireOp",EDGE,"E9.1.3"),sQuery(id+"F0.wireOp",EDGE,"E10.trimOffspring"),sQuery(id+"F0.wireOp",EDGE,"E11.trimOffspring")])],"isStart":false}),makeQuery(id+"F13.opExtrude","CAP_FACE",FACE,{"disambiguationData":[OSD([sQuery(id+"F12.wireOp",EDGE,"E31.0"),sQuery(id+"F12.wireOp",EDGE,"E32.0"),sQuery(id+"F12.wireOp",EDGE,"E34"),sQuery(id+"F12.wireOp",EDGE,"E35")])],"isStart":false}),makeQuery(id+"F13.opExtrude","CAP_FACE",FACE,{"disambiguationData":[OSD([sQuery(id+"F12.wireOp",EDGE,"E36.1.0"),sQuery(id+"F12.wireOp",EDGE,"E36.1.1"),sQuery(id+"F12.wireOp",EDGE,"E36.1.2"),sQuery(id+"F12.wireOp",EDGE,"E36.1.3")])],"isStart":false}),makeQuery(id+"F13.opExtrude","CAP_FACE",FACE,{"disambiguationData":[OSD([sQuery(id+"F12.wireOp",EDGE,"E36.2.0"),sQuery(id+"F12.wireOp",EDGE,"E36.2.1"),sQuery(id+"F12.wireOp",EDGE,"E36.2.2"),sQuery(id+"F12.wireOp",EDGE,"E36.2.3")])],"isStart":false}),makeQuery(id+"F13.opExtrude","CAP_FACE",FACE,{"disambiguationData":[OSD([sQuery(id+"F12.wireOp",EDGE,"E37.1.3.0"),sQuery(id+"F12.wireOp",EDGE,"E37.3.3.0"),sQuery(id+"F12.wireOp",EDGE,"E37.6.3.0"),sQuery(id+"F12.wireOp",EDGE,"E37.9.3.0")])],"isStart":false}),makeQuery(id+"F13.opExtrude","CAP_FACE",FACE,{"disambiguationData":[OSD([sQuery(id+"F12.wireOp",EDGE,"E38.1.4.0"),sQuery(id+"F12.wireOp",EDGE,"E38.3.4.0"),sQuery(id+"F12.wireOp",EDGE,"E38.6.4.0"),sQuery(id+"F12.wireOp",EDGE,"E38.9.4.0")])],"isStart":false}),makeQuery(id+"F13.opExtrude","CAP_FACE",FACE,{"disambiguationData":[OSD([sQuery(id+"F12.wireOp",EDGE,"E38.1.5.0"),sQuery(id+"F12.wireOp",EDGE,"E38.3.5.0"),sQuery(id+"F12.wireOp",EDGE,"E38.6.5.0"),sQuery(id+"F12.wireOp",EDGE,"E38.9.5.0")])],"isStart":false}),makeQuery(id+"F13.opExtrude","CAP_FACE",FACE,{"disambiguationData":[OSD([sQuery(id+"F12.wireOp",EDGE,"E39.1.6.0"),sQuery(id+"F12.wireOp",EDGE,"E39.3.6.0"),sQuery(id+"F12.wireOp",EDGE,"E39.6.6.0"),sQuery(id+"F12.wireOp",EDGE,"E39.9.6.0")])],"isStart":false}),makeQuery(id+"F13.opExtrude","CAP_FACE",FACE,{"disambiguationData":[OSD([sQuery(id+"F12.wireOp",EDGE,"E39.1.7.0"),sQuery(id+"F12.wireOp",EDGE,"E39.3.7.0"),sQuery(id+"F12.wireOp",EDGE,"E39.6.7.0"),sQuery(id+"F12.wireOp",EDGE,"E39.9.7.0")])],"isStart":false})]}),makeQuery(id+"F17.opExtrude","SWEPT_FACE",FACE,{"disambiguationData":[OSD([sQuery(id+"F16.wireOp",EDGE,"E42.bottom")])]})]});var subQ2=makeQuery(id+"F20.imprint","INTERSECT",VERTEX,{"disambiguationData":[OD(0.0)],"derivedFrom":[subQ1,subQ0]});Q4=makeQuery(id+"F20.imprint","IMPRINT",FACE,{"disambiguationData":[TD([[makeQuery(id+"F20.imprint","IMPRINT",EDGE,{"disambiguationData":[TD([[subQ2,-1.0]])],"derivedFrom":subQ0}),1.0]])]});}
            extrude(context, id + "F21", {"entities" : qUnion([Q0, Q1, Q2, Q3, Q4]), "operationType" : NewBodyOperationType.ADD, "oppositeDirection" : true, "depth" : 5 * mm, "offsetDistance" : 25.4 * mm});
        }
    });
